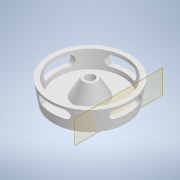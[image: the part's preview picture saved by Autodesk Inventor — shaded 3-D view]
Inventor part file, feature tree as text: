
AUTODESK INVENTOR PART (.ipt)
format: ipt  version: 2022 (Build 260153000, 153)  size: 192,512 bytes
history: native  units: in
note: dims shown in document units (in); Inventor stores cm internally (conversion verified against a paired STEP export)
features: sketch x2, revolve x1, plane x1, extrude x1, pattern_circular x1
ambient origin geometry x8: Origin, YZ Plane, XZ Plane, XY Plane, X Axis, Y Axis, Z Axis, Center Point
bodies: Solid1 (feature_tree)
feature tree (6):
  revolve  "Revolution1"  [1 undecoded]
  plane  "Work Plane1"
  extrude  "Extrusion1"  TaperAngle=360.0deg  [1 undecoded]
  pattern_circular  "Circular Pattern1"  [2 undecoded]
  sketch  "Sketch1"  dims[d0=0.6919in d1=0.374in]
  sketch  "Sketch2"  dims[d2=0.6299in d3=360.0deg d4=0.1969in d5=0.1575in d6=0.1673in d7=1.384in d8=0.0in d9=1.5748in d10=360.0deg d12=0.0787in d13=0.0984in d14=0.1969in d15=0.1575in d16=0.0787in d18=0.1181in d19=0.2756in d20=0.5in]
note: 4 required parameter values undecoded (feature->parameter linkage not recoverable at this tier; creation-order binding heuristic only, values carry confidence <= 0.55)